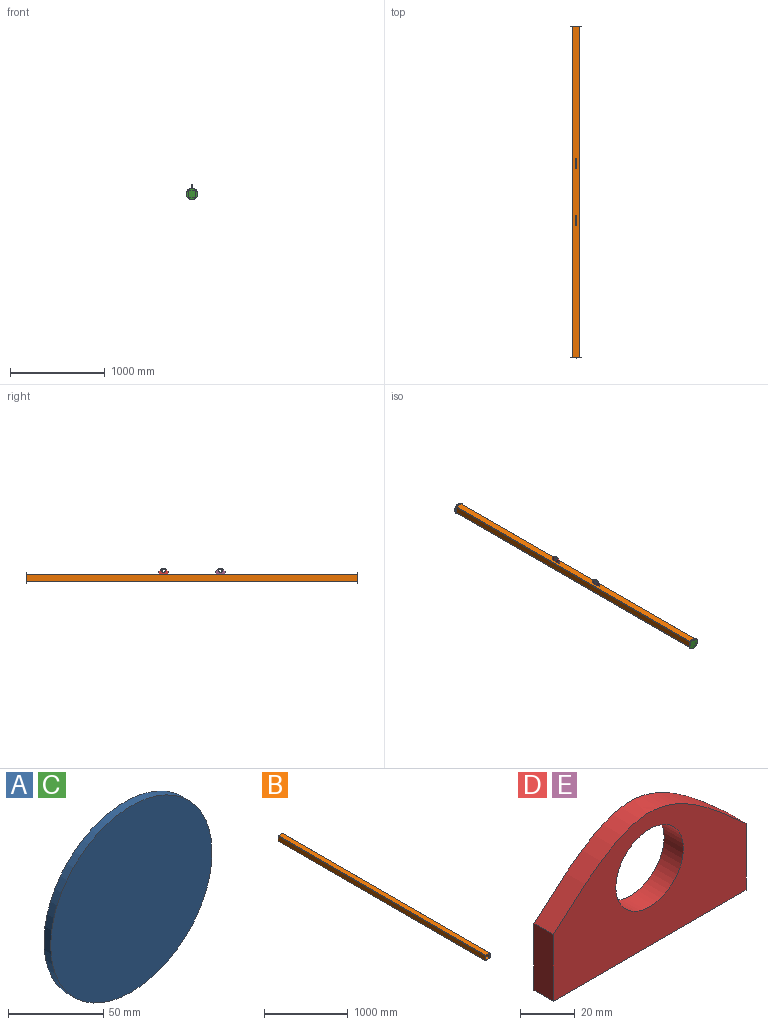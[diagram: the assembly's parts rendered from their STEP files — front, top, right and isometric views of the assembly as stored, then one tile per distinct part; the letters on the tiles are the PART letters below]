
ASSEMBLY  parts=5 mates=4
PART A: 3 faces, bbox 120x5x120 mm
  f0: cylinder r=60mm len=120mm, axis (0,1,0), area 1885mm2, adj f1,f2
  f1: plane 120x120mm, normal (0,-1,0), area 11309.7mm2, adj f0
  f2: plane 120x120mm, normal (0,1,0), area 11309.7mm2, adj f0
PART B: 18 faces, bbox 80x3500x80 mm
  f0: plane 3500x64mm, normal (0,0,-1), area 224000mm2, adj f8,f9,f10,f13
  f1: plane 3500x64mm, normal (-1,0,0), area 224000mm2, adj f8,f9,f10,f11
  f2: plane 3500x64mm, normal (0,0,1), area 224000mm2, adj f8,f9,f11,f12
  f3: plane 3500x70mm, normal (1,0,0), area 245000mm2, adj f8,f9,f14,f17
  f4: plane 3500x70mm, normal (0,0,1), area 245000mm2, adj f8,f9,f14,f15
  f5: plane 3500x70mm, normal (-1,0,0), area 245000mm2, adj f8,f9,f15,f16
  f6: plane 3500x70mm, normal (0,0,-1), area 245000mm2, adj f8,f9,f16,f17
  f7: plane 3500x64mm, normal (1,0,0), area 224000mm2, adj f8,f9,f12,f13
  f8: plane 80x80mm, normal (0,-1,0), area 1486.3mm2, adj f0,f1,f2,f3,f4,f5,f6,f7
  f9: plane 80x80mm, normal (0,1,0), area 1486.3mm2, adj f0,f1,f2,f3,f4,f5,f6,f7
  f10: cylinder r=3mm len=3500mm, axis (0,1,0), area 16493.4mm2, adj f0,f1,f8,f9
  f11: cylinder r=3mm len=3500mm, axis (0,-1,0), area 16493.4mm2, adj f1,f2,f8,f9
  f12: cylinder r=3mm len=3500mm, axis (0,1,0), area 16493.4mm2, adj f2,f7,f8,f9
  f13: cylinder r=3mm len=3500mm, axis (0,-1,0), area 16493.4mm2, adj f0,f7,f8,f9
  f14: cylinder r=5mm len=3500mm, axis (0,-1,0), area 27488.9mm2, adj f3,f4,f8,f9
  f15: cylinder r=5mm len=3500mm, axis (0,1,0), area 27488.9mm2, adj f4,f5,f8,f9
  f16: cylinder r=5mm len=3500mm, axis (0,-1,0), area 27488.9mm2, adj f5,f6,f8,f9
  f17: cylinder r=5mm len=3500mm, axis (0,1,0), area 27488.9mm2, adj f3,f6,f8,f9
PART C: same geometry as A
PART D: 7 faces, bbox 100x10x61.6 mm
  f0: extruded ~100x30mm, area 1190.6mm2, adj f1,f3,f5,f6
  f1: plane 30x10mm, normal (-1,0,0), area 300mm2, adj f0,f2,f5,f6
  f2: plane 100x10mm, normal (0,0,-1), area 1000mm2, adj f1,f3,f5,f6
  f3: plane 30x10mm, normal (1,0,0), area 300mm2, adj f0,f2,f5,f6
  f4: cylinder r=17.5mm len=35mm, axis (0,1,0), area 1099.6mm2, adj f5,f6
  f5: plane 100x61.56mm, normal (0,-1,0), area 3912.9mm2, adj f0,f1,f2,f3,f4
  f6: plane 100x61.56mm, normal (0,1,0), area 3912.9mm2, adj f0,f1,f2,f3,f4
PART E: same geometry as D
PLACE A t=(-776.7,2238.4,-1231.01)mm
PLACE B t=(-776.7,2233.4,-1231.01)mm
PLACE C t=(-776.7,-1266.6,-1231.01)mm
PLACE D rot(axis=(0,0,1),90deg) t=(-781.7,783.4,-1176.01)mm
PLACE E rot(axis=(0,0,1),90deg) t=(-781.7,183.4,-1176.01)mm
MATE fastened D.f2 <-> B.f4  axis (0,0,-1) through (-776.7,783.4,-1191.01)mm
MATE fastened B.f9 <-> A.f0  axis (0,1,0) through (-776.7,2233.4,-1231.01)mm
MATE fastened E.f2 <-> B.f4  axis (0,0,-1) through (-776.7,183.4,-1191.01)mm
MATE fastened B.f8 <-> C.f0  axis (0,-1,0) through (-776.7,-1266.6,-1231.01)mm
